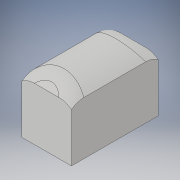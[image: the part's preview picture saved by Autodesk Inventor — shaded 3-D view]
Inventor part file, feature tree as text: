
AUTODESK INVENTOR PART (.ipt)
format: ipt  version: 2019 (Build 230136000, 136)  size: 147,968 bytes
history: native  units: mm
features: fillet x2, other x1, extrude x1, chamfer x1, sketch x1
ambient origin geometry x8: Origin, YZ Plane, XZ Plane, XY Plane, X Axis, Y Axis, Z Axis, Center Point
bodies: Body1 (feature_tree)
feature tree (6):
  other  "Твердое тело1"
  extrude  "Выдавливание1"  Depth=4.9mm
  chamfer  "Фаска1"  Distance=4.0mm
  fillet  "Сопряжение1"  Radius=1.0mm
  fillet  "Сопряжение2"  Radius=2.0mm
  sketch  "Эскиз1"
